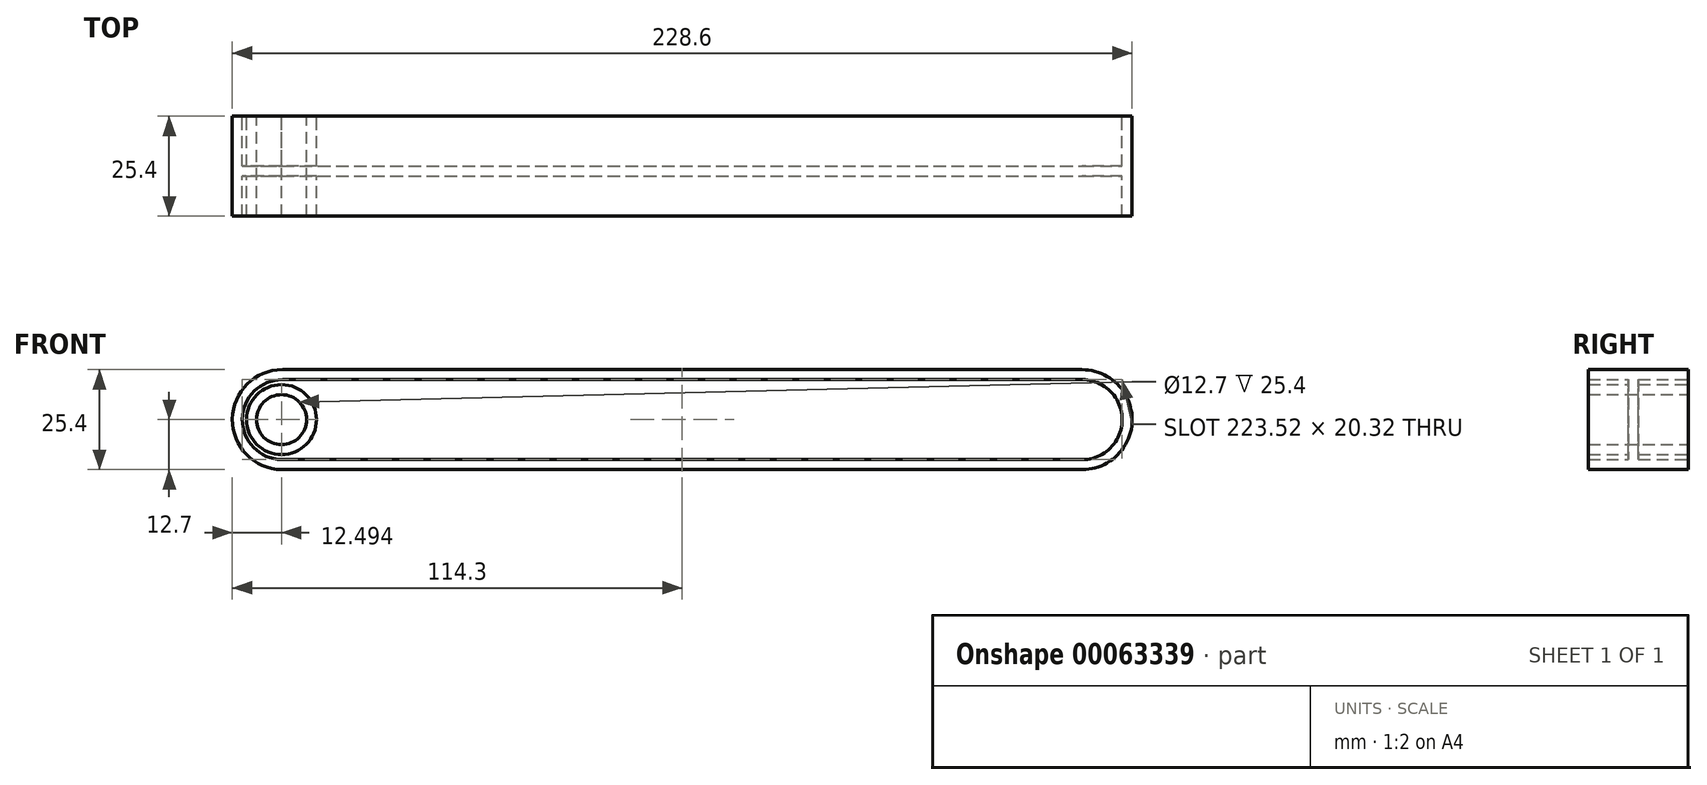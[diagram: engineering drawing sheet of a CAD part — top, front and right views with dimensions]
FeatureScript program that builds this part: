
annotation { "Feature Type Name" : "Feature", "Feature Type Description" : "" }
export const myFeature = defineFeature(function(context is Context, id is Id, definition is map)
    precondition{}
    {
        {
            var Q0;
            Q0=qCreatedBy(makeId("Front.planeOp"),FACE);
            var sketch = newSketch(context, id + "F0", { "sketchPlane" : qUnion([Q0])});
            skArc(sketch, "E0", {"start": v(-152.37, 12.7) * mm, "mid": v(-165.1, -0.1) * mm, "end": v(-152.2, -12.7) * mm});
            skArc(sketch, "E1", {"start": v(50.8, -12.7) * mm, "mid": v(63.5, 0.01) * mm, "end": v(50.77, 12.7) * mm});
            skLineSegment(sketch, "E2", {"start": v(-152.37, 12.7) * mm, "end": v(50.77, 12.7) * mm});
            skLineSegment(sketch, "E3", {"start": v(-152.6, -12.7) * mm, "end": v(50.8, -12.7) * mm});
            skSolve(sketch);
        }
        {
            var Q0;
            {var subQ5=sQuery(id+"F0.wireOp",EDGE,"E1");Q0=makeQuery(id+"F0.imprint","IMPRINT",FACE,{"disambiguationData":[TD([[makeQuery(id+"F0.imprint","IMPRINT",EDGE,{"derivedFrom":subQ5}),1.0]])]});}
            extrude(context, id + "F1", {"entities" : qUnion([Q0]), "depth" : 12.7 * mm});
        }
        {
            var Q0;
            Q0=makeQuery(id+"F1.opExtrude","CAP_FACE",FACE,{"disambiguationData":[OSD([sQuery(id+"F0.wireOp",EDGE,"E0"),sQuery(id+"F0.wireOp",EDGE,"E1"),sQuery(id+"F0.wireOp",EDGE,"E2"),sQuery(id+"F0.wireOp",EDGE,"E3")])],"isStart":true});
            var sketch = newSketch(context, id + "F2", { "sketchPlane" : qUnion([Q0])});
            skCircle(sketch, "E4", {"center": v(152.6, 0) * mm, "radius": 6.35 * mm});
            skSolve(sketch);
        }
        {
            var Q0;
            Q0=makeQuery(id+"F2.imprint","IMPRINT",FACE,{"disambiguationData":[TD([[makeQuery(id+"F2.imprint","IMPRINT",EDGE,{"derivedFrom":sQuery(id+"F2.wireOp",EDGE,"E4")}),1.0]])]});
            extrude(context, id + "F3", {"entities" : qUnion([Q0]), "operationType" : NewBodyOperationType.REMOVE, "oppositeDirection" : true, "depth" : 25.4 * mm});
        }
        {
            var Q0;
            Q0=makeQuery(id+"F1.opExtrude","CAP_FACE",FACE,{"disambiguationData":[OSD([sQuery(id+"F0.wireOp",EDGE,"E0"),sQuery(id+"F0.wireOp",EDGE,"E1"),sQuery(id+"F0.wireOp",EDGE,"E2"),sQuery(id+"F0.wireOp",EDGE,"E3")])],"isStart":false});
            shell(context, id + "F4", {"entities" : qUnion([Q0]), "thickness" : 2.54 * mm});
        }
        {
            var Q0;
            Q0=makeQuery(id+"F1.opExtrude","CAP_FACE",FACE,{"disambiguationData":[OSD([sQuery(id+"F0.wireOp",EDGE,"E0"),sQuery(id+"F0.wireOp",EDGE,"E1"),sQuery(id+"F0.wireOp",EDGE,"E2"),sQuery(id+"F0.wireOp",EDGE,"E3")])],"isStart":true});
            extrude(context, id + "F5", {"entities" : qUnion([Q0]), "operationType" : NewBodyOperationType.ADD, "depth" : 12.7 * mm});
        }
        {
            var Q0;
            Q0=makeQuery(id+"F5.opExtrude","CAP_FACE",FACE,{"disambiguationData":[OSD([sQuery(id+"F0.wireOp",EDGE,"E0"),sQuery(id+"F0.wireOp",EDGE,"E1"),sQuery(id+"F0.wireOp",EDGE,"E2"),sQuery(id+"F0.wireOp",EDGE,"E3")])],"isStart":false});
            shell(context, id + "F6", {"entities" : qUnion([Q0]), "thickness" : 2.54 * mm});
        }
    });
